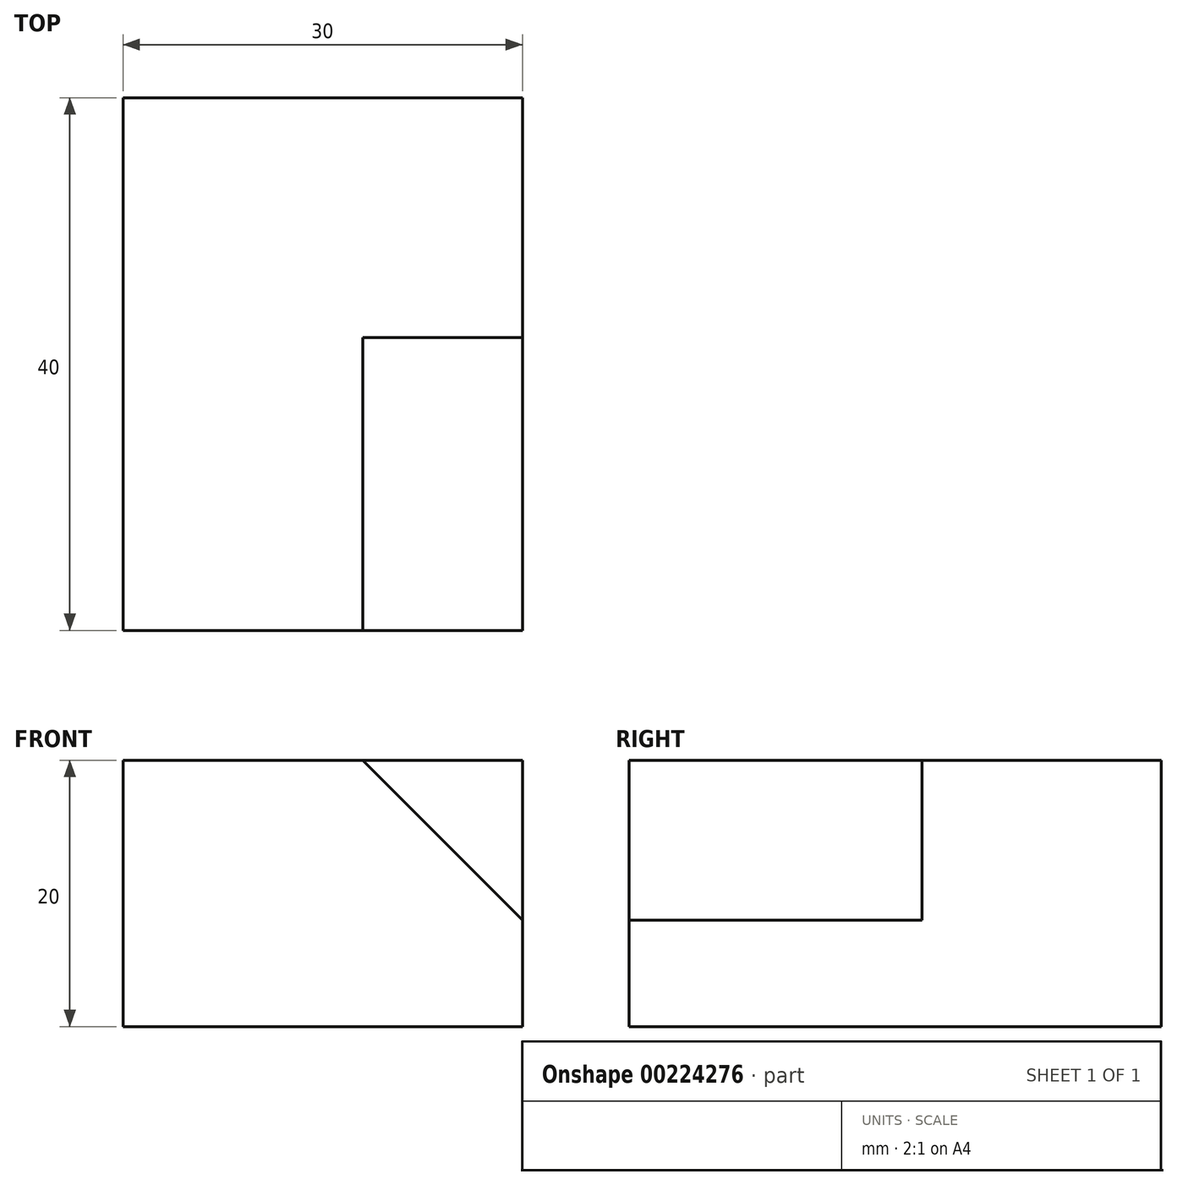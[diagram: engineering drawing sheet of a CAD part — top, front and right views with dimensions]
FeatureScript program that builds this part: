
annotation { "Feature Type Name" : "Feature", "Feature Type Description" : "" }
export const myFeature = defineFeature(function(context is Context, id is Id, definition is map)
    precondition{}
    {
        {
            var Q0;
            Q0=qCreatedBy(makeId("Front.planeOp"),FACE);
            var sketch = newSketch(context, id + "F0", { "sketchPlane" : qUnion([Q0])});
            skLineSegment(sketch, "E0.bottom", {"start": v(0, 0) * mm, "end": v(30, 0) * mm});
            skLineSegment(sketch, "E0.top", {"start": v(0, 20) * mm, "end": v(30, 20) * mm});
            skLineSegment(sketch, "E0.left", {"start": v(0, 0) * mm, "end": v(0, 20) * mm});
            skLineSegment(sketch, "E0.right", {"start": v(30, 0) * mm, "end": v(30, 20) * mm});
            skPoint(sketch, "E1", {"position": v(30, 20) * mm});
            skPoint(sketch, "E2", {"position": v(18, 20) * mm});
            skPoint(sketch, "E3", {"position": v(30, 8) * mm});
            skLineSegment(sketch, "E4", {"start": v(18, 20) * mm, "end": v(30, 8) * mm});
            skSolve(sketch);
        }
        {
            var Q0;
            {var subQ1=sQuery(id+"F0.wireOp",EDGE,"E0.bottom");Q0=makeQuery(id+"F0.imprint","IMPRINT",FACE,{"disambiguationData":[TD([[makeQuery(id+"F0.imprint","IMPRINT",EDGE,{"derivedFrom":subQ1}),1.0]])]});}
            var Q1;
            {var subQ3=sQuery(id+"F0.wireOp",EDGE,"E4");Q1=makeQuery(id+"F0.imprint","IMPRINT",FACE,{"disambiguationData":[TD([[makeQuery(id+"F0.imprint","IMPRINT",EDGE,{"derivedFrom":subQ3}),1.0]])]});}
            extrude(context, id + "F1", {"entities" : qUnion([Q0, Q1]), "oppositeDirection" : true, "depth" : 40 * mm});
        }
        {
            var Q0;
            Q0=qCreatedBy(makeId("Front.planeOp"),FACE);
            var sketch = newSketch(context, id + "F2", { "sketchPlane" : qUnion([Q0])});
            skLineSegment(sketch, "E5", {"start": v(18, 20) * mm, "end": v(30, 8) * mm});
            skLineSegment(sketch, "E6", {"start": v(18, 20) * mm, "end": v(30, 20) * mm});
            skLineSegment(sketch, "E7", {"start": v(30, 20) * mm, "end": v(30, 8) * mm});
            skSolve(sketch);
        }
        {
            var Q0;
            Q0 = qSketchRegion(id + "F2", true);
            var Q1;
            Q1=makeQuery(id+"F1.opExtrude","CAP_FACE",FACE,{"disambiguationData":[OSD([sQuery(id+"F0.wireOp",EDGE,"E0.bottom"),sQuery(id+"F0.wireOp",EDGE,"E0.top"),sQuery(id+"F0.wireOp",EDGE,"E0.left"),sQuery(id+"F0.wireOp",EDGE,"E0.right")])],"isStart":false});
            extrude(context, id + "F3", {"entities" : qUnion([Q0, Q1]), "operationType" : NewBodyOperationType.REMOVE, "oppositeDirection" : true, "depth" : 22 * mm});
        }
    });
